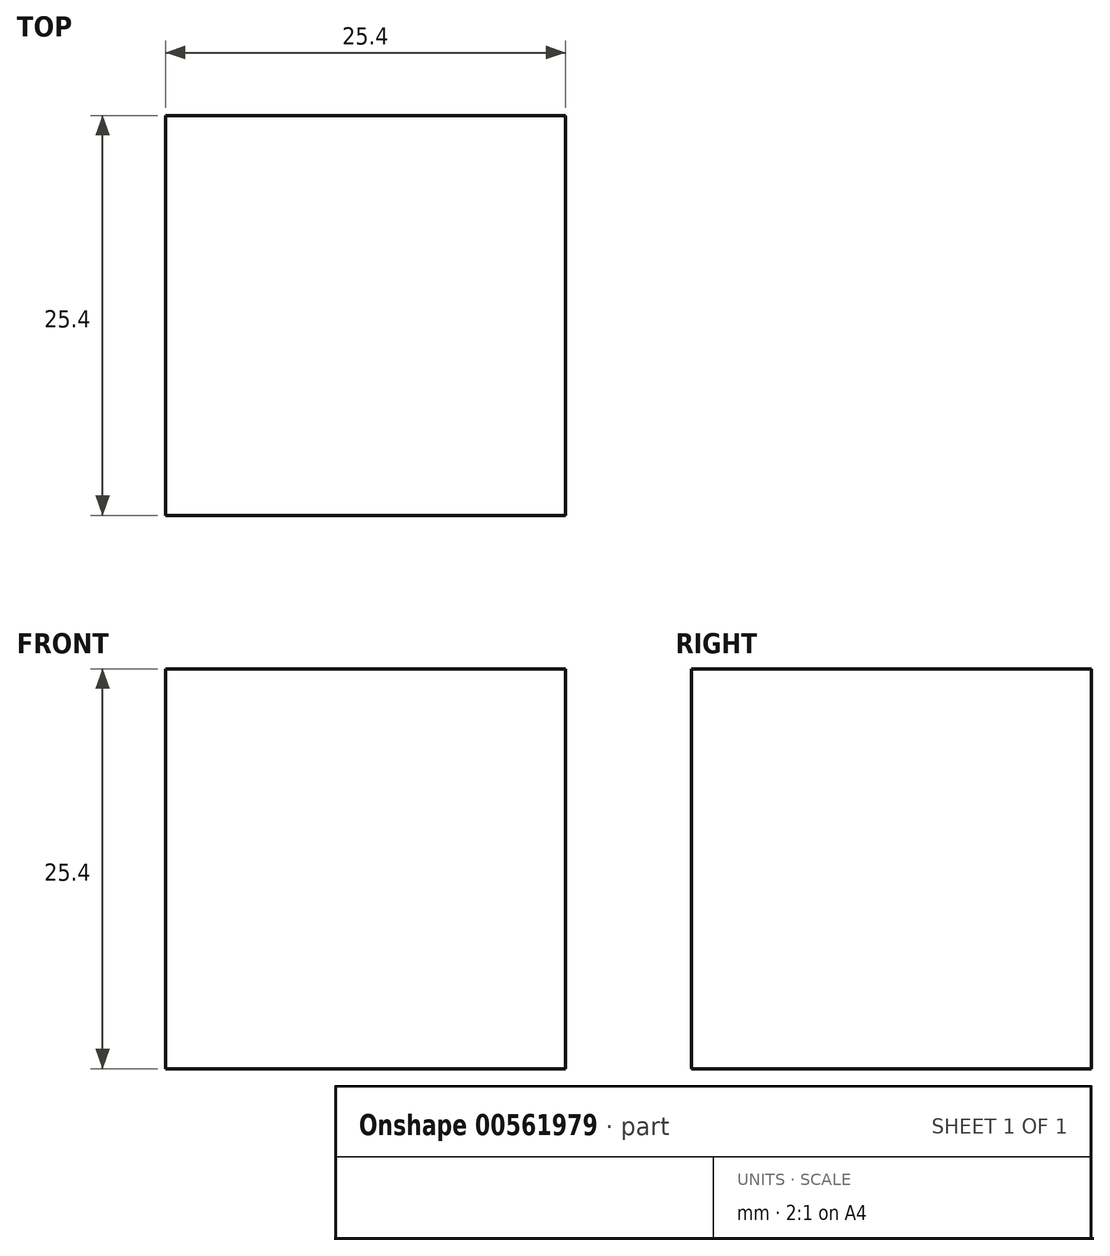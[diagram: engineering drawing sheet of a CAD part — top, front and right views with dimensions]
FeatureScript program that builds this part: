
annotation { "Feature Type Name" : "Feature", "Feature Type Description" : "" }
export const myFeature = defineFeature(function(context is Context, id is Id, definition is map)
    precondition{}
    {
        {
            var Q0;
            Q0=qCreatedBy(makeId("Front.planeOp"),FACE);
            var sketch = newSketch(context, id + "F0", { "sketchPlane" : qUnion([Q0])});
            skLineSegment(sketch, "E0.bottom", {"start": v(-25.4, 36.72) * mm, "end": v(0, 36.72) * mm});
            skLineSegment(sketch, "E0.top", {"start": v(-25.4, 11.32) * mm, "end": v(0, 11.32) * mm});
            skLineSegment(sketch, "E0.left", {"start": v(-25.4, 36.72) * mm, "end": v(-25.4, 11.32) * mm});
            skLineSegment(sketch, "E0.right", {"start": v(0, 36.72) * mm, "end": v(0, 11.32) * mm});
            skSolve(sketch);
        }
        {
            var Q0;
            Q0=makeQuery(id+"F0.imprint","IMPRINT",FACE,{"disambiguationData":[TD([[makeQuery(id+"F0.imprint","IMPRINT",EDGE,{"derivedFrom":sQuery(id+"F0.wireOp",EDGE,"E0.bottom")}),-1.0]])]});
            extrude(context, id + "F1", {"entities" : qUnion([Q0]), "depth" : 25.4 * mm, "offsetDistance" : 25.4 * mm});
        }
    });
